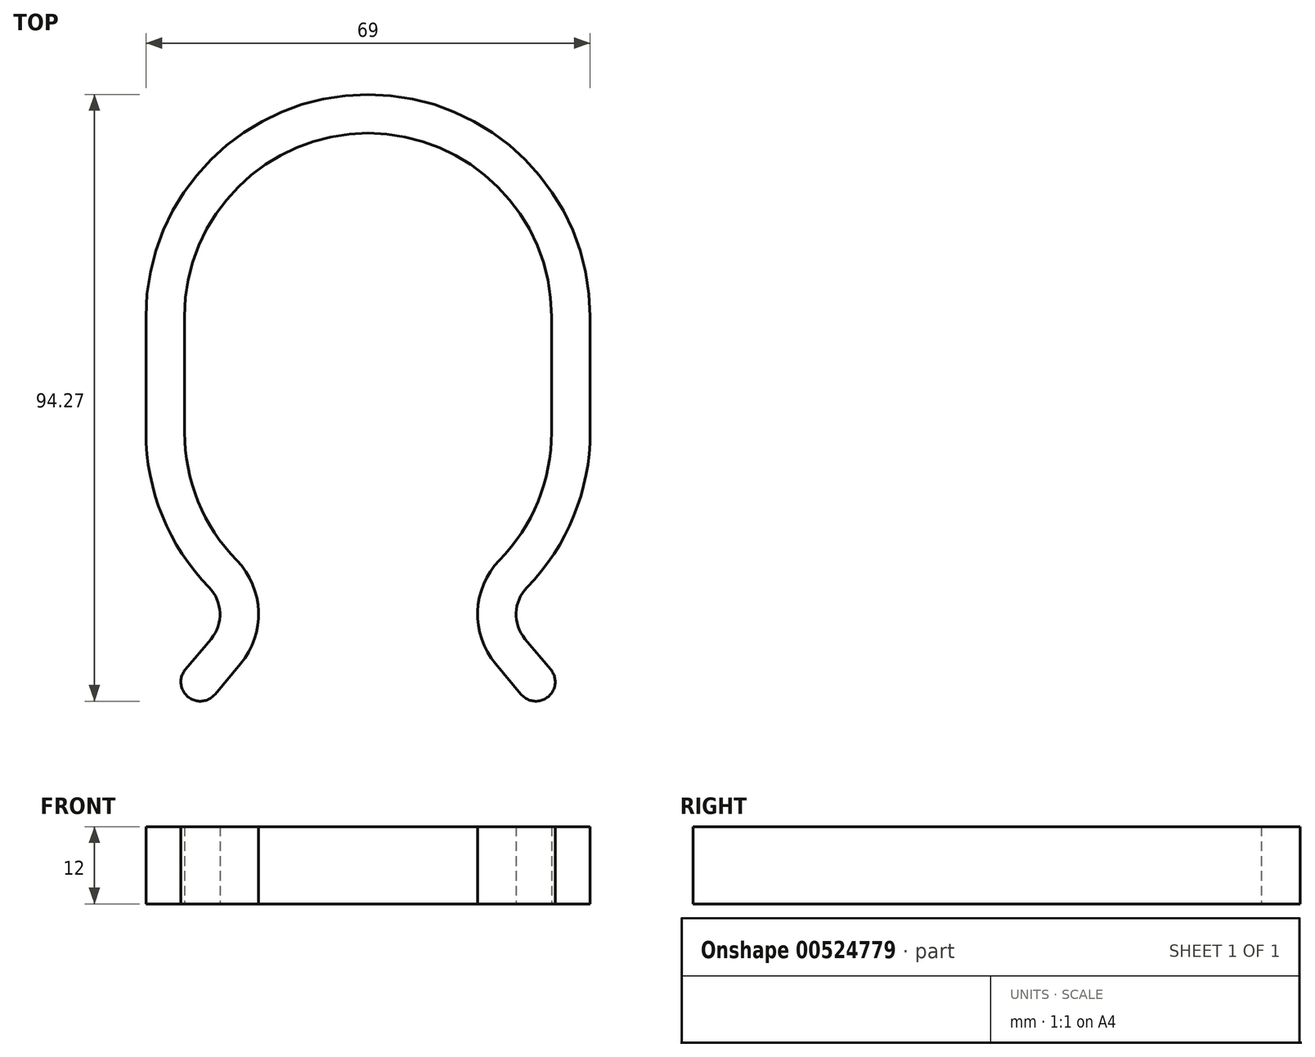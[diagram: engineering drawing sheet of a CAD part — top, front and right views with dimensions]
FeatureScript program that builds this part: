
annotation { "Feature Type Name" : "Feature", "Feature Type Description" : "" }
export const myFeature = defineFeature(function(context is Context, id is Id, definition is map)
    precondition{}
    {
        {
            assignVariable(context, id + "F0", {"variableType" : VariableType.LENGTH, "name" : "t", "lengthValue" : 6 * mm});
        }
        {
            var Q0;
            Q0=qCreatedBy(makeId("Top.planeOp"),FACE);
            var sketch = newSketch(context, id + "F1", { "sketchPlane" : qUnion([Q0])});
            skArc(sketch, "E0", {"start": v(28.5, 0) * mm, "mid": v(0, 28.5) * mm, "end": v(-28.5, 0) * mm});
            skLineSegment(sketch, "E1", {"start": v(-28.5, 0) * mm, "end": v(-28.5, -18) * mm});
            skLineSegment(sketch, "E2", {"start": v(28.5, 0) * mm, "end": v(28.5, -18) * mm});
            skArc(sketch, "E3", {"start": v(-28.5, -18) * mm, "mid": v(-23.87, -33.56) * mm, "end": v(-11.5, -44.08) * mm});
            skArc(sketch, "E4.0", {"start": v(34.5, 0) * mm, "mid": v(0, 34.5) * mm, "end": v(-34.5, 0) * mm});
            skLineSegment(sketch, "E4.1", {"start": v(34.5, 0) * mm, "end": v(34.5, -18) * mm});
            skArc(sketch, "E4.2", {"start": v(-34.5, -18) * mm, "mid": v(-30.84, -33.46) * mm, "end": v(-20.65, -45.64) * mm});
            skLineSegment(sketch, "E4.3", {"start": v(-34.5, 0) * mm, "end": v(-34.5, -18) * mm});
            skLineSegment(sketch, "E5", {"start": v(-20.65, -45.64) * mm, "end": v(-30.3, -57.14) * mm});
            skLineSegment(sketch, "E6.0", {"start": v(-11.5, -44.08) * mm, "end": v(-25.7, -61) * mm});
            skLineSegment(sketch, "E7", {"start": v(-30.3, -57.14) * mm, "end": v(-25.7, -61) * mm});
            skLineSegment(sketch, "E8.MirrorCS", {"start": v(20.65, -45.64) * mm, "end": v(30.3, -57.14) * mm});
            skLineSegment(sketch, "E9.MirrorCS", {"start": v(11.5, -44.08) * mm, "end": v(25.7, -61) * mm});
            skLineSegment(sketch, "E10.MirrorCS", {"start": v(30.3, -57.14) * mm, "end": v(25.7, -61) * mm});
            skArc(sketch, "E11.trimOffspring", {"start": v(11.5, -44.08) * mm, "mid": v(23.87, -33.56) * mm, "end": v(28.5, -18) * mm});
            skArc(sketch, "E12.trimOffspring", {"start": v(20.65, -45.64) * mm, "mid": v(30.84, -33.46) * mm, "end": v(34.5, -18) * mm});
            skSolve(sketch);
        }
        {
            var Q0;
            Q0=makeQuery(id+"F1.imprint","IMPRINT",FACE,{"disambiguationData":[TD([[makeQuery(id+"F1.imprint","IMPRINT",EDGE,{"derivedFrom":sQuery(id+"F1.wireOp",EDGE,"E0")}),-1.0]])]});
            extrude(context, id + "F2", {"entities" : qUnion([Q0]), "flatOperationType" : FlatOperationType.REMOVE, "depth" : getVariable(context, 't') * 2, "offsetDistance" : 25 * mm, "domain" : OperationDomain.MODEL});
        }
        {
            var Q0;
            Q0=makeQuery(id+"F2.opExtrude","SWEPT_EDGE",EDGE,{"disambiguationData":[OSD([sQuery(id+"F1.wireOp",EDGE,"E8.MirrorCS"),sQuery(id+"F1.wireOp",EDGE,"E12.trimOffspring")])]});
            var Q1;
            Q1=makeQuery(id+"F2.opExtrude","SWEPT_EDGE",EDGE,{"disambiguationData":[OSD([sQuery(id+"F1.wireOp",EDGE,"E4.2"),sQuery(id+"F1.wireOp",EDGE,"E5")])]});
            fillet(context, id + "F3", {"entities" : qUnion([Q0, Q1]), "radius" : getVariable(context, 't'), "tangentPropagation" : true, "defaultsChanged" : true, "vertexSettings" : [], "allowEdgeOverflow" : false});
        }
        {
            var Q0;
            Q0=makeQuery(id+"F2.opExtrude","SWEPT_EDGE",EDGE,{"disambiguationData":[OSD([sQuery(id+"F1.wireOp",EDGE,"E3"),sQuery(id+"F1.wireOp",EDGE,"E6.0")])]});
            var Q1;
            Q1=makeQuery(id+"F2.opExtrude","SWEPT_EDGE",EDGE,{"disambiguationData":[OSD([sQuery(id+"F1.wireOp",EDGE,"E9.MirrorCS"),sQuery(id+"F1.wireOp",EDGE,"E11.trimOffspring")])]});
            fillet(context, id + "F4", {"entities" : qUnion([Q0, Q1]), "radius" : getVariable(context, 't') * 2, "tangentPropagation" : true, "defaultsChanged" : true, "vertexSettings" : [], "allowEdgeOverflow" : false});
        }
        {
            var Q0;
            Q0=makeQuery(id+"F2.opExtrude","SWEPT_EDGE",EDGE,{"disambiguationData":[OSD([sQuery(id+"F1.wireOp",EDGE,"E6.0"),sQuery(id+"F1.wireOp",EDGE,"E7")])]});
            var Q1;
            Q1=makeQuery(id+"F2.opExtrude","SWEPT_EDGE",EDGE,{"disambiguationData":[OSD([sQuery(id+"F1.wireOp",EDGE,"E5"),sQuery(id+"F1.wireOp",EDGE,"E7")])]});
            var Q2;
            Q2=makeQuery(id+"F2.opExtrude","SWEPT_EDGE",EDGE,{"disambiguationData":[OSD([sQuery(id+"F1.wireOp",EDGE,"E9.MirrorCS"),sQuery(id+"F1.wireOp",EDGE,"E10.MirrorCS")])]});
            var Q3;
            Q3=makeQuery(id+"F2.opExtrude","SWEPT_EDGE",EDGE,{"disambiguationData":[OSD([sQuery(id+"F1.wireOp",EDGE,"E8.MirrorCS"),sQuery(id+"F1.wireOp",EDGE,"E10.MirrorCS")])]});
            fillet(context, id + "F5", {"entities" : qUnion([Q0, Q1, Q2, Q3]), "radius" : getVariable(context, 't') / 2, "tangentPropagation" : true, "defaultsChanged" : true, "vertexSettings" : [], "allowEdgeOverflow" : false});
        }
    });
